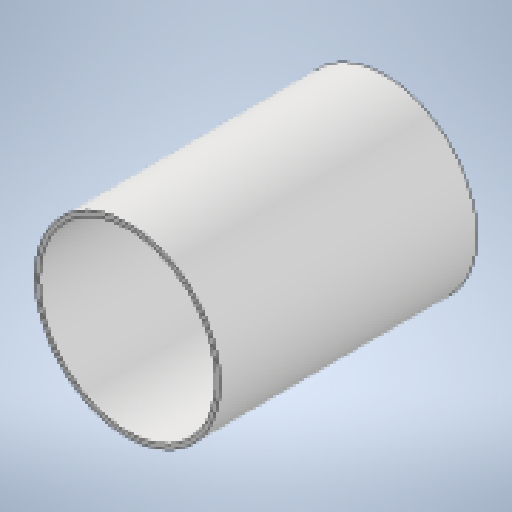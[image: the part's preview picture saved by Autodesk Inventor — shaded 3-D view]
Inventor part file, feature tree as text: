
AUTODESK INVENTOR PART (.ipt)
format: ipt  version: 2025.1 (Build 291241020, 241B)  size: 147,456 bytes
history: native  units: mm
features: extrude x1, sketch x1
ambient origin geometry x8: Origin, YZ Plane, XZ Plane, XY Plane, X Axis, Y Axis, Z Axis, Center Point
bodies: Solid1 (feature_tree)
feature tree (2):
  extrude  "Extrusion1"  Depth=220.0mm
  sketch  "Sketch1"  dims[d0=159.0mm d1=4.0mm d2=220.0mm d3=0.0mm]
